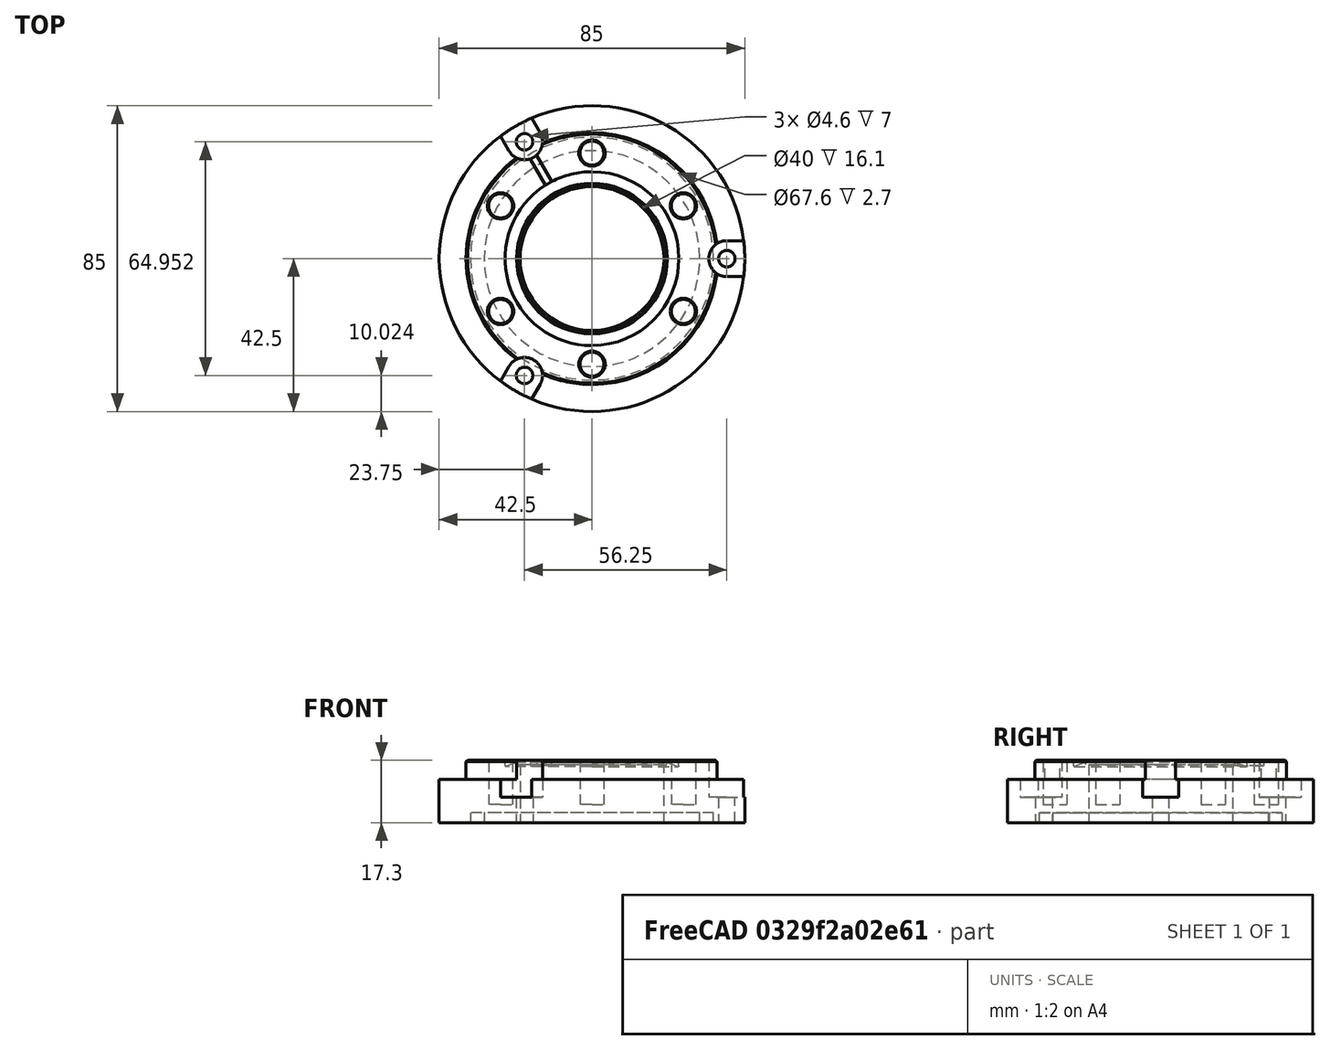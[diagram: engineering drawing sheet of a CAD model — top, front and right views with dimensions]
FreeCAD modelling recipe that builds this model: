
FCSTD DOCUMENT  (FreeCAD 0.21R0.20.1)
Label: PhilipsXL30_FlangeToCF35_CF40_ZeroLengthAdapter
License: All rights reserved
LicenseURL: http://en.wikipedia.org/wiki/All_rights_reserved
objects: TechDraw::DrawViewDimension×34, Part::Cylinder×5, TechDraw::DrawProjGroupItem×4, Part::Compound×3, Part::Cut×3, TechDraw::DrawSVGTemplate×3, TechDraw::DrawPage×3, TechDraw::DrawProjGroup×2, TechDraw::DrawViewSection×2, Part::Feature×1, App::Link×1, Part::MultiFuse×1, TechDraw::DrawViewPart×1
note: 13 computed .brp shape members not serialized (recipe doc carries the construction recipe); baked Part::Feature solids carry a one-line shape summary decoded from their .brp
EXTERNAL_REF file=PhilipsXL30_Blindflange.FCStd obj=Cut001_solid

FEATURE [Part::Feature] Solid  label="CF35 Flange"
  Placement = pos=(0,0,4.6) rot=(1,0,0;1.5708rad)
  shape: bbox 70 x 70 x 12.7 mm, 58 faces (baked)
FEATURE [App::Link] Link  label="Cut001 (Solid)"
  LinkedObject = -> <external PhilipsXL30_Blindflange.FCStd>#Cut001_solid
FEATURE [Part::Cylinder] Cylinder004  label="Zylinder004"
  Angle = 360
  AttacherType = Attacher::AttachEngine3D
  FirstAngle = 0
  Height = 12
  Placement = pos=(37.5,0,7) rot=(0,0,1;0rad)
  Radius = 5
  SecondAngle = 0
FEATURE [Part::Cylinder] Cylinder005  label="Zylinder005"
  Angle = 360
  AttacherType = Attacher::AttachEngine3D
  FirstAngle = 0
  Height = 12
  Placement = pos=(37.5,0,7) rot=(0,0,1;0rad)
  Radius = 5
  SecondAngle = 0
FEATURE [Part::Compound] Compound
  Links = -> [Cylinder005]
  Placement = pos=(0,0,0) rot=(0,0,1;2.0944rad)
FEATURE [Part::Cylinder] Cylinder006  label="Zylinder006"
  Angle = 360
  AttacherType = Attacher::AttachEngine3D
  FirstAngle = 0
  Height = 12
  Placement = pos=(37.5,0,7) rot=(0,0,1;0rad)
  Radius = 5
  SecondAngle = 0
FEATURE [Part::Compound] Compound001
  Links = -> [Cylinder006]
  Placement = pos=(0,0,0) rot=(0,0,1;4.18879rad)
FEATURE [Part::Compound] Compound002
  Links = -> [Compound001,Cylinder004,Compound]
FEATURE [Part::Cut] Cut
  Base = -> Solid
  Tool = -> Compound002
FEATURE [Part::Cylinder] Cylinder  label="Zylinder"
  Angle = 360
  AttacherType = Attacher::AttachEngine3D
  FirstAngle = 0
  Height = 50
  Placement = pos=(0,0,-1) rot=(0,0,1;0rad)
  Radius = 20
  SecondAngle = 0
FEATURE [Part::Cylinder] Cylinder007  label="Zylinder007"
  Angle = 360
  AttacherType = Attacher::AttachEngine3D
  FirstAngle = 0
  Height = 12.5
  Placement = pos=(0,0,5) rot=(0,0,1;0rad)
  Radius = 34.95
  SecondAngle = 0
FEATURE [Part::Cut] Cut001
  Base = -> Link
  Tool = -> Cylinder007
FEATURE [Part::MultiFuse] Fusion
  Shapes = -> [Cut,Cut001]
FEATURE [Part::Cut] Cut002
  Base = -> Fusion
  Tool = -> Cylinder
FEATURE [TechDraw::DrawSVGTemplate] Template
  EditableTexts = Designed_by_Name=Thomas Spielauer; Drawing_number=Drawing number; FC-Date=2023-06-20; FC-SC=mm; FC-SH=01/03; FC-Title=Philipps XL30 compatible; Subtitle=Flange to CF35/CF40 ZLA
  Height = 210
  Orientation = 1
  Width = 297
FEATURE [TechDraw::DrawProjGroupItem] ProjItem  label="Front"
  CoarseView = false
  Direction = (0,0,1)
  Focus = 100
  HardHidden = false
  IsoCount = 0
  IsoHidden = false
  IsoVisible = false
  LockPosition = true
  Perspective = false
  Rotation = 0
  RotationVector = (-1,0,0)
  ScaleType = 2
  SeamHidden = false
  SeamVisible = true
  SmoothHidden = false
  SmoothVisible = true
  Source = -> [Cut002]
  Type = 0
  X = 0
  XDirection = (-1,0,0)
  Y = 0
FEATURE [TechDraw::DrawProjGroupItem] ProjItem001  label="Right"
  CoarseView = false
  Direction = (-1,0,1e-16)
  Focus = 100
  HardHidden = false
  IsoCount = 0
  IsoHidden = false
  IsoVisible = false
  LockPosition = false
  Perspective = false
  Rotation = 0
  RotationVector = (1,0,0)
  ScaleType = 2
  SeamHidden = false
  SeamVisible = true
  SmoothHidden = false
  SmoothVisible = true
  Source = -> [Cut002]
  Type = 2
  X = -80.7301
  XDirection = (-1e-16,0,-1)
  Y = 0
FEATURE [TechDraw::DrawProjGroupItem] ProjItem002  label="Rear"
  CoarseView = false
  Direction = (0,0,-1)
  Focus = 100
  HardHidden = false
  IsoCount = 0
  IsoHidden = false
  IsoVisible = false
  LockPosition = false
  Perspective = false
  Rotation = 0
  RotationVector = (1,0,0)
  ScaleType = 2
  SeamHidden = false
  SeamVisible = true
  SmoothHidden = false
  SmoothVisible = true
  Source = -> [Cut002]
  Type = 3
  X = 106.615
  XDirection = (1,0,0)
  Y = 0
FEATURE [TechDraw::DrawProjGroup] ProjGroup
  Anchor = -> ProjItem
  AutoDistribute = false
  LockPosition = false
  ProjectionType = 0
  Rotation = 0
  ScaleType = 0
  Source = -> [Cut002]
  Views = -> [ProjItem,ProjItem001,ProjItem002]
  X = 122.402
  Y = 132.382
  spacingX = 5
  spacingY = 0
FEATURE [TechDraw::DrawViewDimension] Dimension
  AngleOverride = false
  Arbitrary = false
  ArbitraryTolerances = false
  EqualTolerance = true
  ExtensionAngle = 0
  FormatSpec = %.2w
  FormatSpecOverTolerance = %+.2w
  FormatSpecUnderTolerance = %+.2w
  Inverted = false
  LineAngle = 0
  LockPosition = false
  MeasureType = 1
  OverTolerance = 0
  References2D = -> [ProjItem001]
  Rotation = 0
  ScaleType = 0
  TheoreticalExact = false
  Type = 0
  UnderTolerance = 0
  X = 0.981859
  Y = 56.666
FEATURE [TechDraw::DrawViewDimension] Dimension001
  AngleOverride = false
  Arbitrary = false
  ArbitraryTolerances = false
  EqualTolerance = true
  ExtensionAngle = 0
  FormatSpec = %.2w
  FormatSpecOverTolerance = %+.2w
  FormatSpecUnderTolerance = %+.2w
  Inverted = false
  LineAngle = 0
  LockPosition = false
  MeasureType = 1
  OverTolerance = 0
  References2D = -> [ProjItem001]
  Rotation = 0
  ScaleType = 0
  TheoreticalExact = false
  Type = 0
  UnderTolerance = 0
  X = -7.37827
  Y = 63.3396
FEATURE [TechDraw::DrawViewDimension] Dimension002
  AngleOverride = false
  Arbitrary = false
  ArbitraryTolerances = false
  EqualTolerance = true
  ExtensionAngle = 0
  FormatSpec = ⌀%.2w
  FormatSpecOverTolerance = %+.2w
  FormatSpecUnderTolerance = %+.2w
  Inverted = false
  LineAngle = 0
  LockPosition = false
  MeasureType = 1
  OverTolerance = 0
  References2D = -> [ProjItem]
  Rotation = 0
  ScaleType = 0
  TheoreticalExact = false
  Type = 5
  UnderTolerance = 0
  X = -30.7018
  Y = 44.8387
FEATURE [TechDraw::DrawViewDimension] Dimension003
  AngleOverride = false
  Arbitrary = false
  ArbitraryTolerances = false
  EqualTolerance = true
  ExtensionAngle = 0
  FormatSpec = ⌀%.2w
  FormatSpecOverTolerance = %+.2w
  FormatSpecUnderTolerance = %+.2w
  Inverted = false
  LineAngle = 0
  LockPosition = false
  MeasureType = 1
  OverTolerance = 0
  References2D = -> [ProjItem]
  Rotation = 0
  ScaleType = 0
  TheoreticalExact = false
  Type = 5
  UnderTolerance = 0
  X = -10.7169
  Y = 58.1384
FEATURE [TechDraw::DrawViewDimension] Dimension004
  AngleOverride = false
  Arbitrary = false
  ArbitraryTolerances = false
  EqualTolerance = true
  ExtensionAngle = 0
  FormatSpec = %.2w
  FormatSpecOverTolerance = %+.2w
  FormatSpecUnderTolerance = %+.2w
  Inverted = false
  LineAngle = 0
  LockPosition = false
  MeasureType = 1
  OverTolerance = 0
  References2D = -> [ProjItem]
  Rotation = 0
  ScaleType = 0
  TheoreticalExact = false
  Type = 0
  UnderTolerance = 0
  X = -60.8736
  Y = 12.5448
FEATURE [TechDraw::DrawViewDimension] Dimension005
  AngleOverride = false
  Arbitrary = true
  ArbitraryTolerances = false
  EqualTolerance = true
  ExtensionAngle = 0
  FormatSpec = M6 threading
  FormatSpecOverTolerance = %+.2w
  FormatSpecUnderTolerance = %+.2w
  Inverted = false
  LineAngle = 0
  LockPosition = false
  MeasureType = 1
  OverTolerance = 0
  References2D = -> [ProjItem]
  Rotation = 0
  ScaleType = 0
  TheoreticalExact = false
  Type = 5
  UnderTolerance = 0
  X = -51.9281
  Y = -31.9474
FEATURE [TechDraw::DrawViewDimension] Dimension006
  AngleOverride = false
  Arbitrary = false
  ArbitraryTolerances = false
  EqualTolerance = true
  ExtensionAngle = 0
  FormatSpec = ⌀%.2w
  FormatSpecOverTolerance = %+.2w
  FormatSpecUnderTolerance = %+.2w
  Inverted = false
  LineAngle = 0
  LockPosition = false
  MeasureType = 1
  OverTolerance = 0
  References2D = -> [ProjItem]
  Rotation = 0
  ScaleType = 0
  TheoreticalExact = false
  Type = 5
  UnderTolerance = 0
  X = 5.01616
  Y = 9.12566
FEATURE [TechDraw::DrawViewDimension] Dimension007
  AngleOverride = false
  Arbitrary = false
  ArbitraryTolerances = false
  EqualTolerance = true
  ExtensionAngle = 0
  FormatSpec = ⌀%.2w
  FormatSpecOverTolerance = %+.2w
  FormatSpecUnderTolerance = %+.2w
  Inverted = false
  LineAngle = 0
  LockPosition = false
  MeasureType = 1
  OverTolerance = 0
  References2D = -> [ProjItem]
  Rotation = 0
  ScaleType = 0
  TheoreticalExact = false
  Type = 5
  UnderTolerance = 0
  X = 27.8015
  Y = 48.0484
FEATURE [TechDraw::DrawViewDimension] Dimension008
  AngleOverride = false
  Arbitrary = false
  ArbitraryTolerances = false
  EqualTolerance = true
  ExtensionAngle = 0
  FormatSpec = ⌀%.2w
  FormatSpecOverTolerance = %+.2w
  FormatSpecUnderTolerance = %+.2w
  Inverted = false
  LineAngle = 0
  LockPosition = false
  MeasureType = 1
  OverTolerance = 0
  References2D = -> [ProjItem002]
  Rotation = 0
  ScaleType = 0
  TheoreticalExact = false
  Type = 5
  UnderTolerance = 0
  X = -3.66037
  Y = 57.8453
FEATURE [TechDraw::DrawViewDimension] Dimension009
  AngleOverride = false
  Arbitrary = false
  ArbitraryTolerances = false
  EqualTolerance = true
  ExtensionAngle = 0
  FormatSpec = ⌀%.2w
  FormatSpecOverTolerance = %+.2w
  FormatSpecUnderTolerance = %+.2w
  Inverted = false
  LineAngle = 0
  LockPosition = false
  MeasureType = 1
  OverTolerance = 0
  References2D = -> [ProjItem002]
  Rotation = 0
  ScaleType = 0
  TheoreticalExact = false
  Type = 5
  UnderTolerance = 0
  X = 2.71226
  Y = 55.6152
FEATURE [TechDraw::DrawViewDimension] Dimension010
  AngleOverride = false
  Arbitrary = false
  ArbitraryTolerances = false
  EqualTolerance = true
  ExtensionAngle = 0
  FormatSpec = ⌀%.2w
  FormatSpecOverTolerance = %+.2w
  FormatSpecUnderTolerance = %+.2w
  Inverted = false
  LineAngle = 0
  LockPosition = false
  MeasureType = 1
  OverTolerance = 0
  References2D = -> [ProjItem002]
  Rotation = 0
  ScaleType = 0
  TheoreticalExact = false
  Type = 5
  UnderTolerance = 0
  X = 10.9613
  Y = 55.6046
FEATURE [TechDraw::DrawViewDimension] Dimension011
  AngleOverride = false
  Arbitrary = false
  ArbitraryTolerances = false
  EqualTolerance = true
  ExtensionAngle = 0
  FormatSpec = ⌀%.2w
  FormatSpecOverTolerance = %+.2w
  FormatSpecUnderTolerance = %+.2w
  Inverted = false
  LineAngle = 0
  LockPosition = false
  MeasureType = 1
  OverTolerance = 0
  References2D = -> [ProjItem002]
  Rotation = 0
  ScaleType = 0
  TheoreticalExact = false
  Type = 5
  UnderTolerance = 0
  X = 20.355
  Y = 54.1691
FEATURE [TechDraw::DrawViewDimension] Dimension012
  AngleOverride = false
  Arbitrary = false
  ArbitraryTolerances = false
  EqualTolerance = true
  ExtensionAngle = 0
  FormatSpec = %.2w
  FormatSpecOverTolerance = %+.2w
  FormatSpecUnderTolerance = %+.2w
  Inverted = false
  LineAngle = 0
  LockPosition = false
  MeasureType = 1
  OverTolerance = 0
  References2D = -> [ProjItem]
  Rotation = 0
  ScaleType = 0
  TheoreticalExact = false
  Type = 0
  UnderTolerance = 0
  X = 80.5725
  Y = 4.77787
FEATURE [TechDraw::DrawViewDimension] Dimension013
  AngleOverride = false
  Arbitrary = false
  ArbitraryTolerances = false
  EqualTolerance = true
  ExtensionAngle = 0
  FormatSpec = R%.2w
  FormatSpecOverTolerance = %+.2w
  FormatSpecUnderTolerance = %+.2w
  Inverted = false
  LineAngle = 0
  LockPosition = false
  MeasureType = 1
  OverTolerance = 0
  References2D = -> [ProjItem]
  Rotation = 0
  ScaleType = 0
  TheoreticalExact = false
  Type = 4
  UnderTolerance = 0
  X = 8.24155
  Y = 57.3473
FEATURE [TechDraw::DrawViewDimension] Dimension014
  AngleOverride = false
  Arbitrary = false
  ArbitraryTolerances = false
  EqualTolerance = true
  ExtensionAngle = 0
  FormatSpec = R%.2w
  FormatSpecOverTolerance = %+.2w
  FormatSpecUnderTolerance = %+.2w
  Inverted = false
  LineAngle = 0
  LockPosition = false
  MeasureType = 1
  OverTolerance = 0
  References2D = -> [ProjItem002]
  Rotation = 0
  ScaleType = 0
  TheoreticalExact = false
  Type = 4
  UnderTolerance = 0
  X = 33.6299
  Y = 47.4253
FEATURE [TechDraw::DrawViewDimension] Dimension015
  AngleOverride = false
  Arbitrary = false
  ArbitraryTolerances = false
  EqualTolerance = true
  ExtensionAngle = 0
  FormatSpec = %.2w
  FormatSpecOverTolerance = %+.2w
  FormatSpecUnderTolerance = %+.2w
  Inverted = false
  LineAngle = 0
  LockPosition = false
  MeasureType = 1
  OverTolerance = 0
  References2D = -> [ProjItem]
  Rotation = 0
  ScaleType = 0
  TheoreticalExact = false
  Type = 6
  UnderTolerance = 0
  X = 49.8347
  Y = 0.653999
FEATURE [TechDraw::DrawViewDimension] Dimension016
  AngleOverride = false
  Arbitrary = false
  ArbitraryTolerances = false
  EqualTolerance = true
  ExtensionAngle = 0
  FormatSpec = %.2w
  FormatSpecOverTolerance = %+.2w
  FormatSpecUnderTolerance = %+.2w
  Inverted = false
  LineAngle = 0
  LockPosition = false
  MeasureType = 1
  OverTolerance = 0
  References2D = -> [ProjItem002]
  Rotation = 0
  ScaleType = 0
  TheoreticalExact = false
  Type = 6
  UnderTolerance = 0
  X = -6.5506
  Y = -20.9661
FEATURE [TechDraw::DrawPage] Page
  KeepUpdated = true
  NextBalloonIndex = 1
  ProjectionType = 0
  Template = -> Template
  Views = -> [ProjGroup,Dimension,Dimension001,Dimension002,Dimension003,Dimension004,Dimension005,Dimension006,Dimension007,Dimension008,Dimension009,Dimension010,Dimension011,Dimension012,Dimension013,Dimension014,Dimension015,Dimension016]
FEATURE [TechDraw::DrawSVGTemplate] Template001
  EditableTexts = Designed_by_Name=Thomas Spielauer; FC-Date=2023-06-20; FC-SC=mm; FC-SH=02/03; FC-Title=Philipps XL30 compatible; Subtitle=Flange to CF35/CF40 ZLA
  Height = 210
  Orientation = 1
  Width = 297
FEATURE [TechDraw::DrawViewPart] View
  CoarseView = false
  Direction = (0,0,1)
  Focus = 100
  HardHidden = false
  IsoCount = 0
  IsoHidden = false
  IsoVisible = false
  LockPosition = false
  Perspective = false
  Rotation = 0
  ScaleType = 0
  SeamHidden = false
  SeamVisible = true
  SmoothHidden = false
  SmoothVisible = true
  Source = -> [Cut002]
  X = 62.9312
  XDirection = (-1,0,0)
  Y = 144.932
FEATURE [TechDraw::DrawViewSection] SectionView  label="Section  - "
  BaseView = -> View
  CoarseView = false
  CutSurfaceDisplay = 2
  Direction = (1,0,0)
  FileGeomPattern = <path>
  FileHatchPattern = <path>
  Focus = 100
  FuseBeforeCut = false
  HardHidden = false
  HatchScale = 1
  IsoCount = 0
  IsoHidden = false
  IsoVisible = false
  LockPosition = false
  NameGeomPattern = Diamond
  Perspective = false
  Rotation = 0
  Scale = 1.3
  ScaleType = 2
  SeamHidden = false
  SeamVisible = true
  SectionDirection = 0
  SectionNormal = (1,0,0)
  SectionOrigin = (0,0,8.65)
  SmoothHidden = false
  SmoothVisible = true
  Source = -> [Cut002]
  X = 173.121
  XDirection = (0,0,1)
  Y = 139.77
FEATURE [TechDraw::DrawViewDimension] Dimension017
  AngleOverride = false
  Arbitrary = false
  ArbitraryTolerances = false
  EqualTolerance = true
  ExtensionAngle = 0
  FormatSpec = %.2w
  FormatSpecOverTolerance = %+.2w
  FormatSpecUnderTolerance = %+.2w
  Inverted = false
  LineAngle = 0
  LockPosition = false
  MeasureType = 1
  OverTolerance = 0
  References2D = -> [SectionView]
  Rotation = 0
  ScaleType = 0
  TheoreticalExact = false
  Type = 0
  UnderTolerance = 0
  X = -26.2186
  Y = 2.66861
FEATURE [TechDraw::DrawViewDimension] Dimension018
  AngleOverride = false
  Arbitrary = false
  ArbitraryTolerances = false
  EqualTolerance = true
  ExtensionAngle = 0
  FormatSpec = %.2w
  FormatSpecOverTolerance = %+.2w
  FormatSpecUnderTolerance = %+.2w
  Inverted = false
  LineAngle = 0
  LockPosition = false
  MeasureType = 1
  OverTolerance = 0
  References2D = -> [SectionView]
  Rotation = 0
  ScaleType = 0
  TheoreticalExact = false
  Type = 0
  UnderTolerance = 0
  X = -26.0803
  Y = 37.3692
FEATURE [TechDraw::DrawViewDimension] Dimension019
  AngleOverride = false
  Arbitrary = false
  ArbitraryTolerances = false
  EqualTolerance = true
  ExtensionAngle = 0
  FormatSpec = %.2w
  FormatSpecOverTolerance = %+.2w
  FormatSpecUnderTolerance = %+.2w
  Inverted = false
  LineAngle = 0
  LockPosition = false
  MeasureType = 1
  OverTolerance = 0
  References2D = -> [SectionView]
  Rotation = 0
  ScaleType = 0
  TheoreticalExact = false
  Type = 0
  UnderTolerance = 0
  X = -42.6925
  Y = 43.2029
FEATURE [TechDraw::DrawViewDimension] Dimension020
  AngleOverride = false
  Arbitrary = false
  ArbitraryTolerances = false
  EqualTolerance = true
  ExtensionAngle = 0
  FormatSpec = %.2w (M6 threading)
  FormatSpecOverTolerance = %+.2w
  FormatSpecUnderTolerance = %+.2w
  Inverted = false
  LineAngle = 0
  LockPosition = false
  MeasureType = 1
  OverTolerance = 0
  References2D = -> [SectionView]
  Rotation = 0
  ScaleType = 0
  TheoreticalExact = false
  Type = 0
  UnderTolerance = 0
  X = 65.4737
  Y = 34.128
FEATURE [TechDraw::DrawViewDimension] Dimension021
  AngleOverride = false
  Arbitrary = false
  ArbitraryTolerances = false
  EqualTolerance = true
  ExtensionAngle = 0
  FormatSpec = %.2w (CF40 flange)
  FormatSpecOverTolerance = %+.2w
  FormatSpecUnderTolerance = %+.2w
  Inverted = false
  LineAngle = 0
  LockPosition = false
  MeasureType = 1
  OverTolerance = 0
  References2D = -> [SectionView]
  Rotation = 0
  ScaleType = 0
  TheoreticalExact = false
  Type = 0
  UnderTolerance = 0
  X = 42.1175
  Y = 2.08838
FEATURE [TechDraw::DrawViewDimension] Dimension022
  AngleOverride = false
  Arbitrary = false
  ArbitraryTolerances = false
  EqualTolerance = true
  ExtensionAngle = 0
  FormatSpec = %.2w (CF40 knife)
  FormatSpecOverTolerance = %+.2w
  FormatSpecUnderTolerance = %+.2w
  Inverted = false
  LineAngle = 0
  LockPosition = false
  MeasureType = 1
  OverTolerance = 0
  References2D = -> [SectionView]
  Rotation = 0
  ScaleType = 0
  TheoreticalExact = false
  Type = 0
  UnderTolerance = 0
  X = 34.7995
  Y = 2.25667
FEATURE [TechDraw::DrawViewDimension] Dimension023
  AngleOverride = false
  Arbitrary = false
  ArbitraryTolerances = false
  EqualTolerance = true
  ExtensionAngle = 0
  FormatSpec = %.2w
  FormatSpecOverTolerance = %+.2w
  FormatSpecUnderTolerance = %+.2w
  Inverted = false
  LineAngle = 0
  LockPosition = false
  MeasureType = 1
  OverTolerance = 0
  References2D = -> [SectionView]
  Rotation = 0
  ScaleType = 0
  TheoreticalExact = false
  Type = 0
  UnderTolerance = 0
  X = -4.13131
  Y = -67.649
FEATURE [TechDraw::DrawViewDimension] Dimension024
  AngleOverride = false
  Arbitrary = false
  ArbitraryTolerances = false
  EqualTolerance = true
  ExtensionAngle = 0
  FormatSpec = %.2w
  FormatSpecOverTolerance = %+.2w
  FormatSpecUnderTolerance = %+.2w
  Inverted = false
  LineAngle = 0
  LockPosition = false
  MeasureType = 1
  OverTolerance = 0
  References2D = -> [SectionView]
  Rotation = 0
  ScaleType = 0
  TheoreticalExact = false
  Type = 0
  UnderTolerance = 0
  X = 7.2924
  Y = -67.7595
FEATURE [TechDraw::DrawViewDimension] Dimension025
  AngleOverride = false
  Arbitrary = false
  ArbitraryTolerances = false
  EqualTolerance = true
  ExtensionAngle = 0
  FormatSpec = %.2w
  FormatSpecOverTolerance = %+.2w
  FormatSpecUnderTolerance = %+.2w
  Inverted = false
  LineAngle = 0
  LockPosition = false
  MeasureType = 1
  OverTolerance = 0
  References2D = -> [SectionView]
  Rotation = 0
  ScaleType = 0
  TheoreticalExact = false
  Type = 0
  UnderTolerance = 0
  X = -49.1232
  Y = 25.0368
FEATURE [TechDraw::DrawViewDimension] Dimension026
  AngleOverride = false
  Arbitrary = false
  ArbitraryTolerances = false
  EqualTolerance = true
  ExtensionAngle = 0
  FormatSpec = %.2w
  FormatSpecOverTolerance = %+.2w
  FormatSpecUnderTolerance = %+.2w
  Inverted = false
  LineAngle = 0
  LockPosition = false
  MeasureType = 1
  OverTolerance = 0
  References2D = -> [SectionView]
  Rotation = 0
  ScaleType = 0
  TheoreticalExact = false
  Type = 0
  UnderTolerance = 0
  X = 27.027
  Y = 51.676
FEATURE [TechDraw::DrawSVGTemplate] Template002
  EditableTexts = Designed_by_Name=Thomas Spielauer; FC-Date=2023-06-20; FC-SC=mm; FC-SH=03/03; FC-Title=Philipps XL30 compatible; Subtitle=Flange to CF35/CF40 ZLA
  Height = 210
  Orientation = 1
  Width = 297
FEATURE [TechDraw::DrawProjGroupItem] ProjItem003  label="Front001"
  CoarseView = false
  Direction = (0,0,1)
  Focus = 100
  HardHidden = false
  IsoCount = 0
  IsoHidden = false
  IsoVisible = false
  LockPosition = true
  Perspective = false
  Rotation = 0
  RotationVector = (-1,0,0)
  ScaleType = 2
  SeamHidden = false
  SeamVisible = true
  SmoothHidden = false
  SmoothVisible = true
  Source = -> [Cut002]
  Type = 0
  X = 0
  XDirection = (2e-16,1,0)
  Y = 0
FEATURE [TechDraw::DrawProjGroup] ProjGroup001
  Anchor = -> ProjItem003
  AutoDistribute = true
  LockPosition = false
  ProjectionType = 0
  Rotation = 0
  ScaleType = 0
  Source = -> [Cut002]
  Views = -> [ProjItem003]
  X = 61.3256
  Y = 143.774
  spacingX = 15
  spacingY = 15
FEATURE [TechDraw::DrawViewSection] SectionView001  label="Section  - 001"
  BaseView = -> ProjItem003
  CoarseView = false
  CutSurfaceDisplay = 2
  Direction = (-2e-16,-1,0)
  FileGeomPattern = <path>
  FileHatchPattern = <path>
  Focus = 100
  FuseBeforeCut = false
  HardHidden = false
  HatchScale = 1
  IsoCount = 0
  IsoHidden = false
  IsoVisible = false
  LockPosition = false
  NameGeomPattern = Diamond
  Perspective = false
  Rotation = 0
  Scale = 1.5
  ScaleType = 2
  SeamHidden = false
  SeamVisible = true
  SectionDirection = 0
  SectionNormal = (-2e-16,-1,0)
  SectionOrigin = (0,0,8.63)
  SmoothHidden = false
  SmoothVisible = true
  Source = -> [Cut002]
  X = 169.536
  XDirection = (0,0,1)
  Y = 132.453
FEATURE [TechDraw::DrawViewDimension] Dimension027
  AngleOverride = false
  Arbitrary = false
  ArbitraryTolerances = false
  EqualTolerance = true
  ExtensionAngle = 0
  FormatSpec = %.2w
  FormatSpecOverTolerance = %+.2w
  FormatSpecUnderTolerance = %+.2w
  Inverted = false
  LineAngle = 0
  LockPosition = false
  MeasureType = 1
  OverTolerance = 0
  References2D = -> [SectionView001]
  Rotation = 0
  ScaleType = 0
  TheoreticalExact = false
  Type = 0
  UnderTolerance = 0
  X = -24.7243
  Y = -55.0396
FEATURE [TechDraw::DrawViewDimension] Dimension028
  AngleOverride = false
  Arbitrary = false
  ArbitraryTolerances = false
  EqualTolerance = true
  ExtensionAngle = 0
  FormatSpec = %.2w
  FormatSpecOverTolerance = %+.2w
  FormatSpecUnderTolerance = %+.2w
  Inverted = false
  LineAngle = 0
  LockPosition = false
  MeasureType = 1
  OverTolerance = 0
  References2D = -> [SectionView001]
  Rotation = 0
  ScaleType = 0
  TheoreticalExact = false
  Type = 0
  UnderTolerance = 0
  X = 29.6201
  Y = -52.8459
FEATURE [TechDraw::DrawViewDimension] Dimension029
  AngleOverride = false
  Arbitrary = false
  ArbitraryTolerances = false
  EqualTolerance = true
  ExtensionAngle = 0
  FormatSpec = %.2w
  FormatSpecOverTolerance = %+.2w
  FormatSpecUnderTolerance = %+.2w
  Inverted = false
  LineAngle = 0
  LockPosition = false
  MeasureType = 1
  OverTolerance = 0
  References2D = -> [SectionView001]
  Rotation = 0
  ScaleType = 0
  TheoreticalExact = false
  Type = 0
  UnderTolerance = 0
  X = 4.53358
  Y = -15.8738
FEATURE [TechDraw::DrawViewDimension] Dimension030
  AngleOverride = false
  Arbitrary = false
  ArbitraryTolerances = false
  EqualTolerance = true
  ExtensionAngle = 0
  FormatSpec = %.2w
  FormatSpecOverTolerance = %+.2w
  FormatSpecUnderTolerance = %+.2w
  Inverted = false
  LineAngle = 0
  LockPosition = false
  MeasureType = 1
  OverTolerance = 0
  References2D = -> [SectionView001]
  Rotation = 0
  ScaleType = 0
  TheoreticalExact = false
  Type = 0
  UnderTolerance = 0
  X = -8.01157
  Y = -15.7909
FEATURE [TechDraw::DrawViewDimension] Dimension031
  AngleOverride = false
  Arbitrary = false
  ArbitraryTolerances = false
  EqualTolerance = true
  ExtensionAngle = 0
  FormatSpec = %.2w
  FormatSpecOverTolerance = %+.2w
  FormatSpecUnderTolerance = %+.2w
  Inverted = false
  LineAngle = 0
  LockPosition = false
  MeasureType = 1
  OverTolerance = 0
  References2D = -> [SectionView]
  Rotation = 0
  ScaleType = 0
  TheoreticalExact = false
  Type = 0
  UnderTolerance = 0
  X = 20.3938
  Y = -35.4781
FEATURE [TechDraw::DrawViewDimension] Dimension032
  AngleOverride = false
  Arbitrary = false
  ArbitraryTolerances = false
  EqualTolerance = true
  ExtensionAngle = 0
  FormatSpec = %.2w (CF40)
  FormatSpecOverTolerance = %+.2w
  FormatSpecUnderTolerance = %+.2w
  Inverted = false
  LineAngle = 0
  LockPosition = false
  MeasureType = 1
  OverTolerance = 0
  References2D = -> [SectionView]
  Rotation = 0
  ScaleType = 0
  TheoreticalExact = false
  Type = 0
  UnderTolerance = 0
  X = 23.9168
  Y = 25.5384
FEATURE [TechDraw::DrawPage] Page001
  KeepUpdated = true
  NextBalloonIndex = 1
  ProjectionType = 0
  Template = -> Template001
  Views = -> [View,SectionView,Dimension017,Dimension018,Dimension019,Dimension020,Dimension021,Dimension022,Dimension023,Dimension024,Dimension025,Dimension026,Dimension031,Dimension032]
FEATURE [TechDraw::DrawViewDimension] Dimension033
  AngleOverride = false
  Arbitrary = false
  ArbitraryTolerances = false
  EqualTolerance = true
  ExtensionAngle = 0
  FormatSpec = %.2w
  FormatSpecOverTolerance = %+.2w
  FormatSpecUnderTolerance = %+.2w
  Inverted = false
  LineAngle = 0
  LockPosition = false
  MeasureType = 1
  OverTolerance = 0
  References2D = -> [SectionView001]
  Rotation = 0
  ScaleType = 0
  TheoreticalExact = false
  Type = 0
  UnderTolerance = 0
  X = -3.975
  Y = 24.6619
FEATURE [TechDraw::DrawPage] Page002
  KeepUpdated = true
  NextBalloonIndex = 1
  ProjectionType = 0
  Template = -> Template002
  Views = -> [ProjGroup001,SectionView001,Dimension027,Dimension028,Dimension029,Dimension030,Dimension033]
note: 4 file-system paths scrubbed to <path> (originals preserved in the JSON sidecar)
